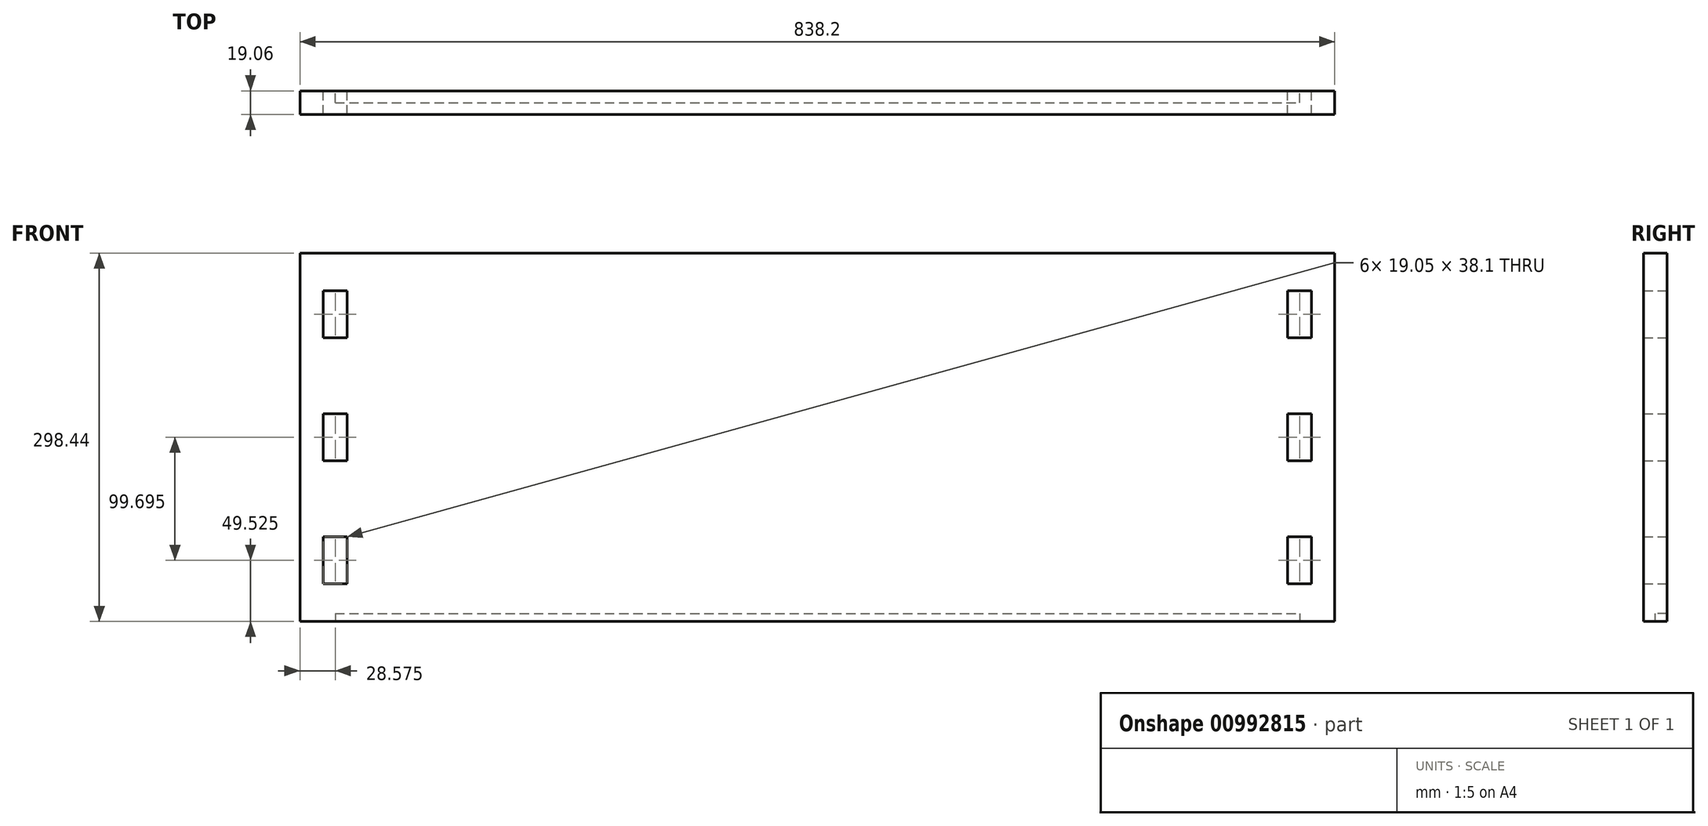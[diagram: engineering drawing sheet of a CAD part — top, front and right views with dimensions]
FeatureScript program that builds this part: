
annotation { "Feature Type Name" : "Feature", "Feature Type Description" : "" }
export const myFeature = defineFeature(function(context is Context, id is Id, definition is map)
    precondition{}
    {
        {
            var Q0;
            Q0=qCreatedBy(makeId("Front.planeOp"),FACE);
            var sketch = newSketch(context, id + "F0", { "sketchPlane" : qUnion([Q0])});
            skLineSegment(sketch, "E0", {"start": v(0, 149.22) * mm, "end": v(0, -149.23) * mm, "construction": true});
            skLineSegment(sketch, "E1", {"start": v(419.1, 0) * mm, "end": v(-419.1, 0) * mm, "construction": true});
            skLineSegment(sketch, "E2.bottom", {"start": v(419.1, 149.22) * mm, "end": v(-419.1, 149.22) * mm});
            skLineSegment(sketch, "E2.top", {"start": v(419.1, -149.22) * mm, "end": v(-419.1, -149.22) * mm});
            skLineSegment(sketch, "E2.left", {"start": v(419.1, 149.22) * mm, "end": v(419.1, -149.22) * mm});
            skLineSegment(sketch, "E2.right", {"start": v(-419.1, 149.22) * mm, "end": v(-419.1, -149.22) * mm});
            skPoint(sketch, "E2.middle", {"position": v(0, 0) * mm});
            skLineSegment(sketch, "E3", {"start": v(-381, 149.22) * mm, "end": v(-381, -149.22) * mm, "construction": true});
            skLineSegment(sketch, "E4", {"start": v(381, 149.22) * mm, "end": v(381, -149.22) * mm, "construction": true});
            skLineSegment(sketch, "E5", {"start": v(-400.05, 149.22) * mm, "end": v(-400.05, -149.22) * mm, "construction": true});
            skLineSegment(sketch, "E6", {"start": v(400.05, 149.22) * mm, "end": v(400.05, -149.22) * mm, "construction": true});
            skLineSegment(sketch, "E7.bottom", {"start": v(381, 118.74) * mm, "end": v(400.05, 118.74) * mm});
            skLineSegment(sketch, "E7.top", {"start": v(381, 80.64) * mm, "end": v(400.05, 80.64) * mm});
            skLineSegment(sketch, "E7.left", {"start": v(381, 118.74) * mm, "end": v(381, 80.64) * mm});
            skLineSegment(sketch, "E7.right", {"start": v(400.05, 118.74) * mm, "end": v(400.05, 80.64) * mm});
            skLineSegment(sketch, "E8.bottom", {"start": v(381, 19.05) * mm, "end": v(400.05, 19.05) * mm});
            skLineSegment(sketch, "E8.top", {"start": v(381, -19.05) * mm, "end": v(400.05, -19.05) * mm});
            skLineSegment(sketch, "E8.left", {"start": v(381, 19.05) * mm, "end": v(381, -19.05) * mm});
            skLineSegment(sketch, "E8.right", {"start": v(400.05, 19.05) * mm, "end": v(400.05, -19.05) * mm});
            skLineSegment(sketch, "E9.bottom", {"start": v(381, -80.64) * mm, "end": v(400.05, -80.64) * mm});
            skLineSegment(sketch, "E9.top", {"start": v(381, -118.74) * mm, "end": v(400.05, -118.74) * mm});
            skLineSegment(sketch, "E9.left", {"start": v(381, -80.64) * mm, "end": v(381, -118.74) * mm});
            skLineSegment(sketch, "E9.right", {"start": v(400.05, -80.64) * mm, "end": v(400.05, -118.74) * mm});
            skLineSegment(sketch, "E10.MirrorCS", {"start": v(-381, -80.64) * mm, "end": v(-381, -118.74) * mm});
            skLineSegment(sketch, "E11.MirrorCS", {"start": v(-400.05, -80.64) * mm, "end": v(-400.05, -118.74) * mm});
            skLineSegment(sketch, "E12.MirrorCS", {"start": v(-381, -118.74) * mm, "end": v(-400.05, -118.74) * mm});
            skLineSegment(sketch, "E13.MirrorCS", {"start": v(-381, -80.64) * mm, "end": v(-400.05, -80.64) * mm});
            skLineSegment(sketch, "E14.MirrorCS", {"start": v(-381, -19.05) * mm, "end": v(-400.05, -19.05) * mm});
            skLineSegment(sketch, "E15.MirrorCS", {"start": v(-381, 19.05) * mm, "end": v(-381, -19.05) * mm});
            skLineSegment(sketch, "E16.MirrorCS", {"start": v(-400.05, 19.05) * mm, "end": v(-400.05, -19.05) * mm});
            skLineSegment(sketch, "E17.MirrorCS", {"start": v(-381, 19.05) * mm, "end": v(-400.05, 19.05) * mm});
            skLineSegment(sketch, "E18.MirrorCS", {"start": v(-381, 80.64) * mm, "end": v(-400.05, 80.64) * mm});
            skLineSegment(sketch, "E19.MirrorCS", {"start": v(-400.05, 118.74) * mm, "end": v(-400.05, 80.64) * mm});
            skLineSegment(sketch, "E20.MirrorCS", {"start": v(-381, 118.74) * mm, "end": v(-400.05, 118.74) * mm});
            skLineSegment(sketch, "E21.MirrorCS", {"start": v(-381, 118.74) * mm, "end": v(-381, 80.64) * mm});
            skSolve(sketch);
        }
        {
            var Q0;
            Q0=makeQuery(id+"F0.imprint","IMPRINT",FACE,{"disambiguationData":[TD([[makeQuery(id+"F0.imprint","IMPRINT",EDGE,{"derivedFrom":sQuery(id+"F0.wireOp",EDGE,"E2.bottom")}),1.0]])]});
            extrude(context, id + "F1", {"entities" : qUnion([Q0]), "endBound" : BoundingType.SYMMETRIC, "depth" : 19.05 * mm, "offsetDistance" : 25.4 * mm});
        }
        {
            var Q0;
            Q0=qCreatedBy(makeId("Right.planeOp"),FACE);
            var sketch = newSketch(context, id + "F2", { "sketchPlane" : qUnion([Q0])});
            skPoint(sketch, "E22.0", {"position": v(9.53, -149.22) * mm});
            skPoint(sketch, "E23.0", {"position": v(-9.53, -149.22) * mm});
            skLineSegment(sketch, "E24.0", {"start": v(-9.53, -149.22) * mm, "end": v(9.52, -149.22) * mm});
            skLineSegment(sketch, "E25.0", {"start": v(9.53, 149.22) * mm, "end": v(9.53, -149.22) * mm});
            skLineSegment(sketch, "E26.bottom", {"start": v(9.53, -149.22) * mm, "end": v(0, -149.22) * mm});
            skLineSegment(sketch, "E26.top", {"start": v(9.53, -142.87) * mm, "end": v(0, -142.87) * mm});
            skLineSegment(sketch, "E26.left", {"start": v(9.53, -149.22) * mm, "end": v(9.53, -142.87) * mm});
            skLineSegment(sketch, "E26.right", {"start": v(0, -149.22) * mm, "end": v(0, -142.87) * mm});
            skSolve(sketch);
        }
        {
            var Q0;
            {var subQ4=sQuery(id+"F2.wireOp",EDGE,"E26.top");Q0=makeQuery(id+"F2.imprint","IMPRINT",FACE,{"disambiguationData":[TD([[makeQuery(id+"F2.imprint","IMPRINT",EDGE,{"derivedFrom":subQ4}),1.0]])]});}
            extrude(context, id + "F3", {"entities" : qUnion([Q0]), "operationType" : NewBodyOperationType.REMOVE, "endBound" : BoundingType.SYMMETRIC, "oppositeDirection" : true, "depth" : 781.05 * mm, "offsetDistance" : 25.4 * mm});
        }
    });
